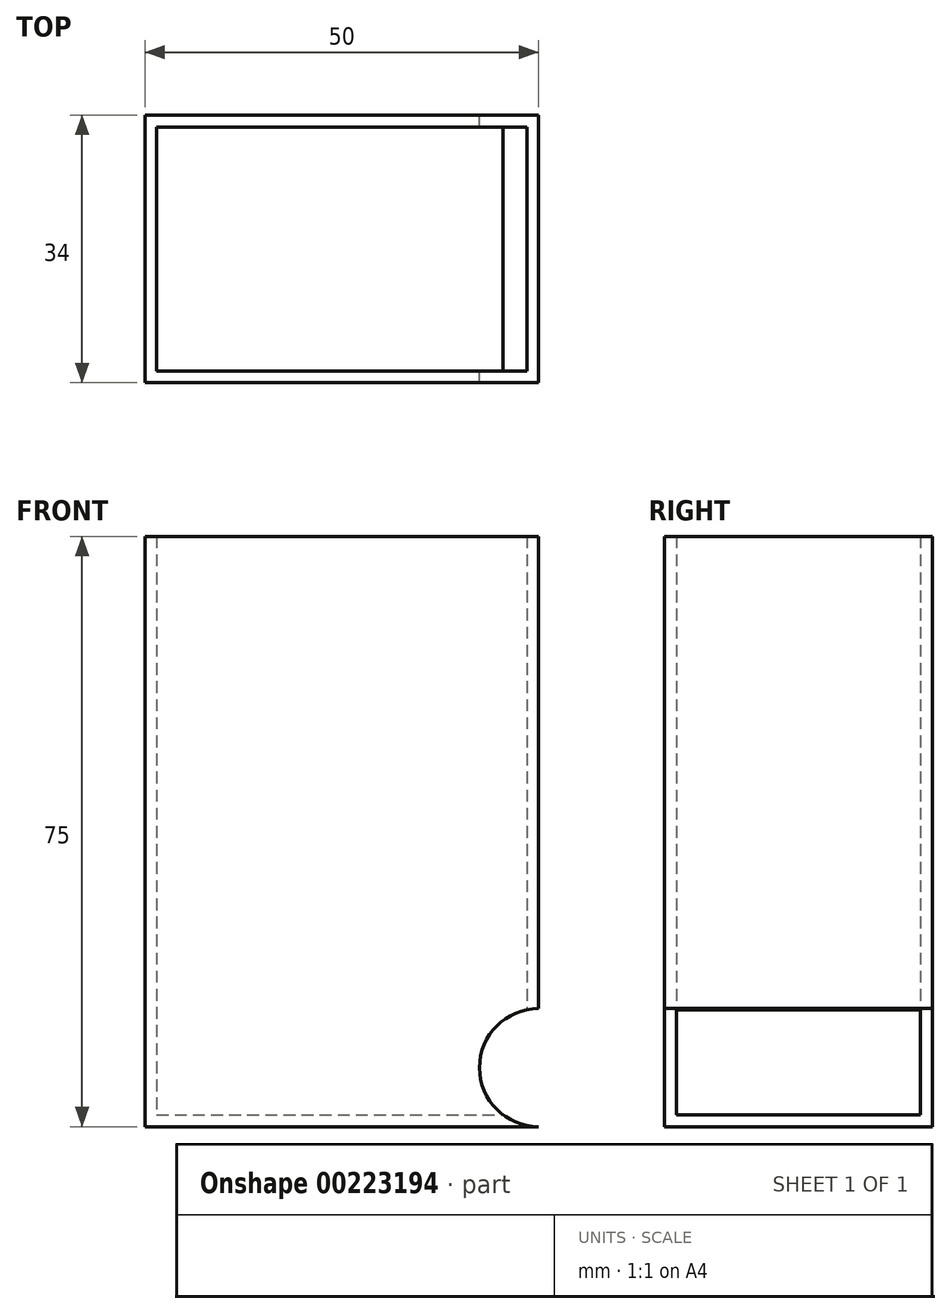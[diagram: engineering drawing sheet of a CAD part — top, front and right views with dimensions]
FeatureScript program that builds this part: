
annotation { "Feature Type Name" : "Feature", "Feature Type Description" : "" }
export const myFeature = defineFeature(function(context is Context, id is Id, definition is map)
    precondition{}
    {
        {
            var Q0;
            Q0=qCreatedBy(makeId("Front.planeOp"),FACE);
            var sketch = newSketch(context, id + "F0", { "sketchPlane" : qUnion([Q0])});
            skLineSegment(sketch, "E0.bottom", {"start": v(-50, 75) * mm, "end": v(0, 75) * mm});
            skLineSegment(sketch, "E0.top", {"start": v(-50, 0) * mm, "end": v(0, 0) * mm});
            skLineSegment(sketch, "E0.left", {"start": v(-50, 75) * mm, "end": v(-50, 0) * mm});
            skLineSegment(sketch, "E0.right", {"start": v(0, 75) * mm, "end": v(0, 0) * mm});
            skArc(sketch, "E1", {"start": v(0, 15) * mm, "mid": v(-7.5, 7.5) * mm, "end": v(0, 0) * mm});
            skSolve(sketch);
        }
        {
            var Q0;
            {var subQ1=sQuery(id+"F0.wireOp",EDGE,"E0.bottom");Q0=makeQuery(id+"F0.imprint","IMPRINT",FACE,{"disambiguationData":[TD([[makeQuery(id+"F0.imprint","IMPRINT",EDGE,{"derivedFrom":subQ1}),-1.0]])]});}
            extrude(context, id + "F1", {"entities" : qUnion([Q0]), "depth" : 34 * mm});
        }
        {
            var Q0;
            Q0=makeQuery(id+"F1.opExtrude","SWEPT_FACE",FACE,{"disambiguationData":[OSD([sQuery(id+"F0.wireOp",EDGE,"E0.bottom")])]});
            var Q1;
            Q1=makeQuery(id+"F1.opExtrude","SWEPT_FACE",FACE,{"disambiguationData":[OSD([sQuery(id+"F0.wireOp",EDGE,"E1")])]});
            shell(context, id + "F2", {"entities" : qUnion([Q0, Q1]), "thickness" : 1.5 * mm});
        }
    });
